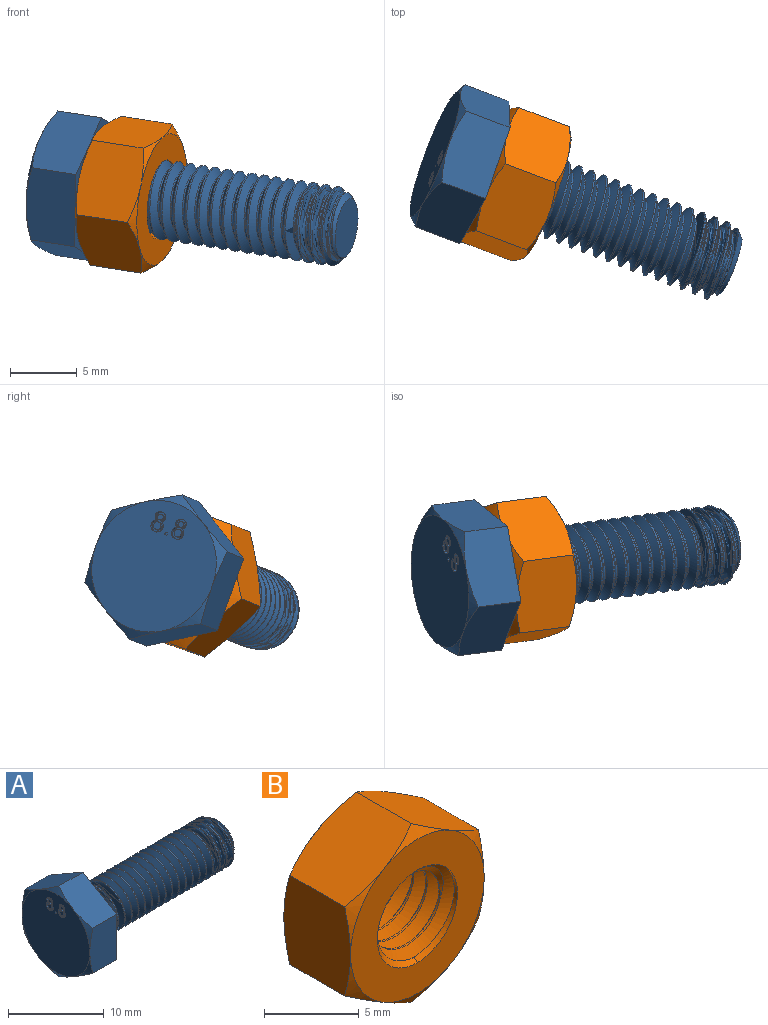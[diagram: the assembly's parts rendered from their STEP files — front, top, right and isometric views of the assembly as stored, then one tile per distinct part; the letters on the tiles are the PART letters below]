
ASSEMBLY  parts=2 mates=1
PART A: 63 faces, bbox 24.8x12x12 mm
  f0: plane 10x10mm, normal (-1,0,0), area 76.1mm2, adj f14,f15,f16,f17,f18,f19,f20,f21
  f1: plane 6.25x4.48mm, normal (0,1,0), area 22.2mm2, adj f2,f6,f13,f16,f17
  f2: plane 5.47x4.48mm, normal (0,0.5,-0.87), area 22.2mm2, adj f1,f3,f13,f15,f16
  f3: plane 5.47x4.48mm, normal (0,-0.5,-0.87), area 22.2mm2, adj f2,f4,f13,f14,f15
  f4: plane 6.25x4.48mm, normal (0,-1,0), area 22.2mm2, adj f3,f5,f13,f14,f19
  f5: plane 5.47x4.48mm, normal (0,-0.5,0.87), area 22.2mm2, adj f4,f6,f13,f18,f19
  f6: plane 5.47x4.48mm, normal (0,0.5,0.87), area 22.2mm2, adj f1,f5,f13,f17,f18
  f7: cylinder r=3mm len=19.25mm, axis (1,0,0), area 45.6mm2, adj f8,f11,f12,f13
  f8: cone r=2.25mm half-angle=45deg, axis (-1,0,0), area 9.5mm2, adj f7,f9,f10,f11,f12
  f9: plane 4.5x4.5mm, normal (1,0,0), area 15.9mm2, adj f8
  f10: bspline ~20.25x4.7mm, area 36.9mm2, adj f8,f11,f12,f13
  f11: bspline ~20.38x6mm, area 248.1mm2, adj f7,f8,f10,f13
  f12: bspline ~20.65x5.99mm, area 247.1mm2, adj f7,f8,f10,f13
  f13: plane 11.93x10.39mm, normal (1,0,0), area 64mm2, adj f1,f2,f3,f4,f5,f6,f7,f10
  f14: cone r=5mm half-angle=60deg, axis (1,0,0), area 2.5mm2, adj f0,f3,f4
  f15: cone r=5mm half-angle=60deg, axis (1,0,0), area 2.5mm2, adj f0,f2,f3
  f16: cone r=5mm half-angle=60deg, axis (1,0,0), area 2.5mm2, adj f0,f1,f2
  f17: cone r=5mm half-angle=60deg, axis (1,0,0), area 2.5mm2, adj f0,f1,f6
  f18: cone r=5mm half-angle=60deg, axis (1,0,0), area 2.5mm2, adj f0,f5,f6
  f19: cone r=5mm half-angle=60deg, axis (1,0,0), area 2.5mm2, adj f0,f4,f5
  f20: extruded ~0.39x0.29mm, area 0.1mm2, adj f0,f21,f27,f28
  f21: extruded ~0.31x0.25mm, area 0.1mm2, adj f0,f20,f22,f28
  f22: extruded ~0.43x0.39mm, area 0.2mm2, adj f0,f21,f23,f28
  f23: extruded ~0.44x0.39mm, area 0.2mm2, adj f0,f22,f24,f28
  f24: extruded ~0.3x0.25mm, area 0.1mm2, adj f0,f23,f25,f28
  f25: extruded ~0.4x0.29mm, area 0.1mm2, adj f0,f24,f26,f28
  f26: extruded ~0.49x0.47mm, area 0.2mm2, adj f0,f25,f27,f28
  f27: extruded ~0.49x0.47mm, area 0.2mm2, adj f0,f20,f26,f28
  f28: plane 1.56x0.99mm, normal (-1,0,0), area 0.8mm2, adj f20,f21,f22,f23,f24,f25,f26,f27
  f29: extruded ~0.25x0.24mm, area 0.1mm2, adj f28,f30,f32,f37
  f30: extruded ~0.25x0.24mm, area 0.1mm2, adj f28,f29,f31,f37
  f31: extruded ~0.25x0.24mm, area 0.1mm2, adj f28,f30,f32,f37
  f32: extruded ~0.25x0.24mm, area 0.1mm2, adj f28,f29,f31,f37
  f33: extruded ~0.29x0.29mm, area 0.1mm2, adj f28,f34,f36,f38
  f34: extruded ~0.3x0.3mm, area 0.1mm2, adj f28,f33,f35,f38
  f35: extruded ~0.3x0.29mm, area 0.1mm2, adj f28,f34,f36,f38
  f36: extruded ~0.3x0.3mm, area 0.1mm2, adj f28,f33,f35,f38
  f37: plane 0.47x0.43mm, normal (-1,0,0), area 0.2mm2, adj f29,f30,f31,f32
  f38: plane 0.59x0.59mm, normal (-1,0,0), area 0.3mm2, adj f33,f34,f35,f36
  f39: plane 0.25x0.2mm, normal (0,0,1), area 0mm2, adj f0,f40,f42,f43
  f40: plane 0.25x0.2mm, normal (0,-1,0), area 0mm2, adj f0,f39,f41,f43
  f41: plane 0.25x0.2mm, normal (0,0,-1), area 0mm2, adj f0,f40,f42,f43
  f42: plane 0.25x0.2mm, normal (0,1,0), area 0mm2, adj f0,f39,f41,f43
  f43: plane 0.2x0.2mm, normal (-1,0,0), area 0mm2, adj f39,f40,f41,f42
  f44: extruded ~0.39x0.29mm, area 0.1mm2, adj f0,f45,f51,f52
  f45: extruded ~0.31x0.25mm, area 0.1mm2, adj f0,f44,f46,f52
  f46: extruded ~0.43x0.39mm, area 0.2mm2, adj f0,f45,f47,f52
  f47: extruded ~0.44x0.39mm, area 0.2mm2, adj f0,f46,f48,f52
  f48: extruded ~0.3x0.25mm, area 0.1mm2, adj f0,f47,f49,f52
  f49: extruded ~0.4x0.29mm, area 0.1mm2, adj f0,f48,f50,f52
  f50: extruded ~0.49x0.47mm, area 0.2mm2, adj f0,f49,f51,f52
  f51: extruded ~0.49x0.47mm, area 0.2mm2, adj f0,f44,f50,f52
  f52: plane 1.56x0.99mm, normal (-1,0,0), area 0.8mm2, adj f44,f45,f46,f47,f48,f49,f50,f51
  f53: extruded ~0.25x0.24mm, area 0.1mm2, adj f52,f54,f56,f61
  f54: extruded ~0.25x0.24mm, area 0.1mm2, adj f52,f53,f55,f61
  f55: extruded ~0.25x0.24mm, area 0.1mm2, adj f52,f54,f56,f61
  f56: extruded ~0.25x0.24mm, area 0.1mm2, adj f52,f53,f55,f61
  f57: extruded ~0.29x0.29mm, area 0.1mm2, adj f52,f58,f60,f62
  f58: extruded ~0.3x0.3mm, area 0.1mm2, adj f52,f57,f59,f62
  f59: extruded ~0.3x0.29mm, area 0.1mm2, adj f52,f58,f60,f62
  f60: extruded ~0.3x0.3mm, area 0.1mm2, adj f52,f57,f59,f62
  f61: plane 0.47x0.43mm, normal (-1,0,0), area 0.2mm2, adj f53,f54,f55,f56
  f62: plane 0.59x0.59mm, normal (-1,0,0), area 0.3mm2, adj f57,f58,f59,f60
PART B: 27 faces, bbox 12x6.1x12 mm
  f0: plane 5.48x5.47mm, normal (-0.5,0,0.87), area 27.1mm2, adj f1,f5,f18,f19,f22,f23
  f1: plane 6.25x5.48mm, normal (-1,0,0), area 27.1mm2, adj f0,f2,f17,f18,f23,f24
  f2: plane 5.48x5.47mm, normal (-0.5,0,-0.87), area 27.1mm2, adj f1,f3,f16,f17,f24,f25
  f3: plane 5.48x5.47mm, normal (0.5,0,-0.87), area 27.1mm2, adj f2,f4,f15,f16,f25,f26
  f4: plane 6.25x5.48mm, normal (1,0,0), area 27.1mm2, adj f3,f5,f15,f20,f21,f26
  f5: plane 5.48x5.47mm, normal (0.5,0,0.87), area 27.1mm2, adj f0,f4,f19,f20,f21,f22
  f6: plane 10x10mm, normal (0,-1,0), area 50.3mm2, adj f8,f14,f15,f16,f17,f18,f19,f20
  f7: plane 10x10mm, normal (0,1,0), area 50.3mm2, adj f9,f14,f21,f22,f23,f24,f25,f26
  f8: cone r=3mm half-angle=45deg, axis (0,-1,0), area 6.8mm2, adj f6,f10,f11,f12,f13
  f9: cone r=3mm half-angle=45deg, axis (0,1,0), area 8mm2, adj f7,f11,f12,f13
  f10: plane 0.38x0.24mm, normal (1,0,0), area 0mm2, adj f8,f13,f14
  f11: cylinder r=2.35mm len=4.7mm, axis (0,-1,0), area 6.8mm2, adj f8,f9,f12,f13
  f12: bspline ~6x6mm, area 55.3mm2, adj f8,f9,f11,f14
  f13: bspline ~6x6mm, area 54.4mm2, adj f8,f9,f10,f11,f14
  f14: cylinder r=3mm len=6mm, axis (0,1,0), area 17.8mm2, adj f6,f7,f10,f12,f13
  f15: cone r=5mm half-angle=60deg, axis (0,1,0), area 2.5mm2, adj f3,f4,f6
  f16: cone r=5mm half-angle=60deg, axis (0,1,0), area 2.5mm2, adj f2,f3,f6
  f17: cone r=5mm half-angle=60deg, axis (0,1,0), area 2.5mm2, adj f1,f2,f6
  f18: cone r=5mm half-angle=60deg, axis (0,1,0), area 2.5mm2, adj f0,f1,f6
  f19: cone r=5mm half-angle=60deg, axis (0,1,0), area 2.5mm2, adj f0,f5,f6
  f20: cone r=5mm half-angle=60deg, axis (0,1,0), area 2.5mm2, adj f4,f5,f6
  f21: cone r=5mm half-angle=60deg, axis (0,-1,0), area 2.5mm2, adj f4,f5,f7
  f22: cone r=5mm half-angle=60deg, axis (0,-1,0), area 2.5mm2, adj f0,f5,f7
  f23: cone r=5mm half-angle=60deg, axis (0,-1,0), area 2.5mm2, adj f0,f1,f7
  f24: cone r=5mm half-angle=60deg, axis (0,-1,0), area 2.5mm2, adj f1,f2,f7
  f25: cone r=5mm half-angle=60deg, axis (0,-1,0), area 2.5mm2, adj f2,f3,f7
  f26: cone r=5mm half-angle=60deg, axis (0,-1,0), area 2.5mm2, adj f3,f4,f7
PLACE A rot(axis=(0.66,0.16,-0.73),29.7deg) t=(15.47,4.49,-4.82)mm
PLACE B rot(axis=(0.67,0.52,-0.54),147deg) t=(10.38,6.41,-4.03)mm
MATE fastened A.f7 <-> B.f8  axis (0.93,-0.35,-0.14) through (8.07,7.29,-3.67)mm
